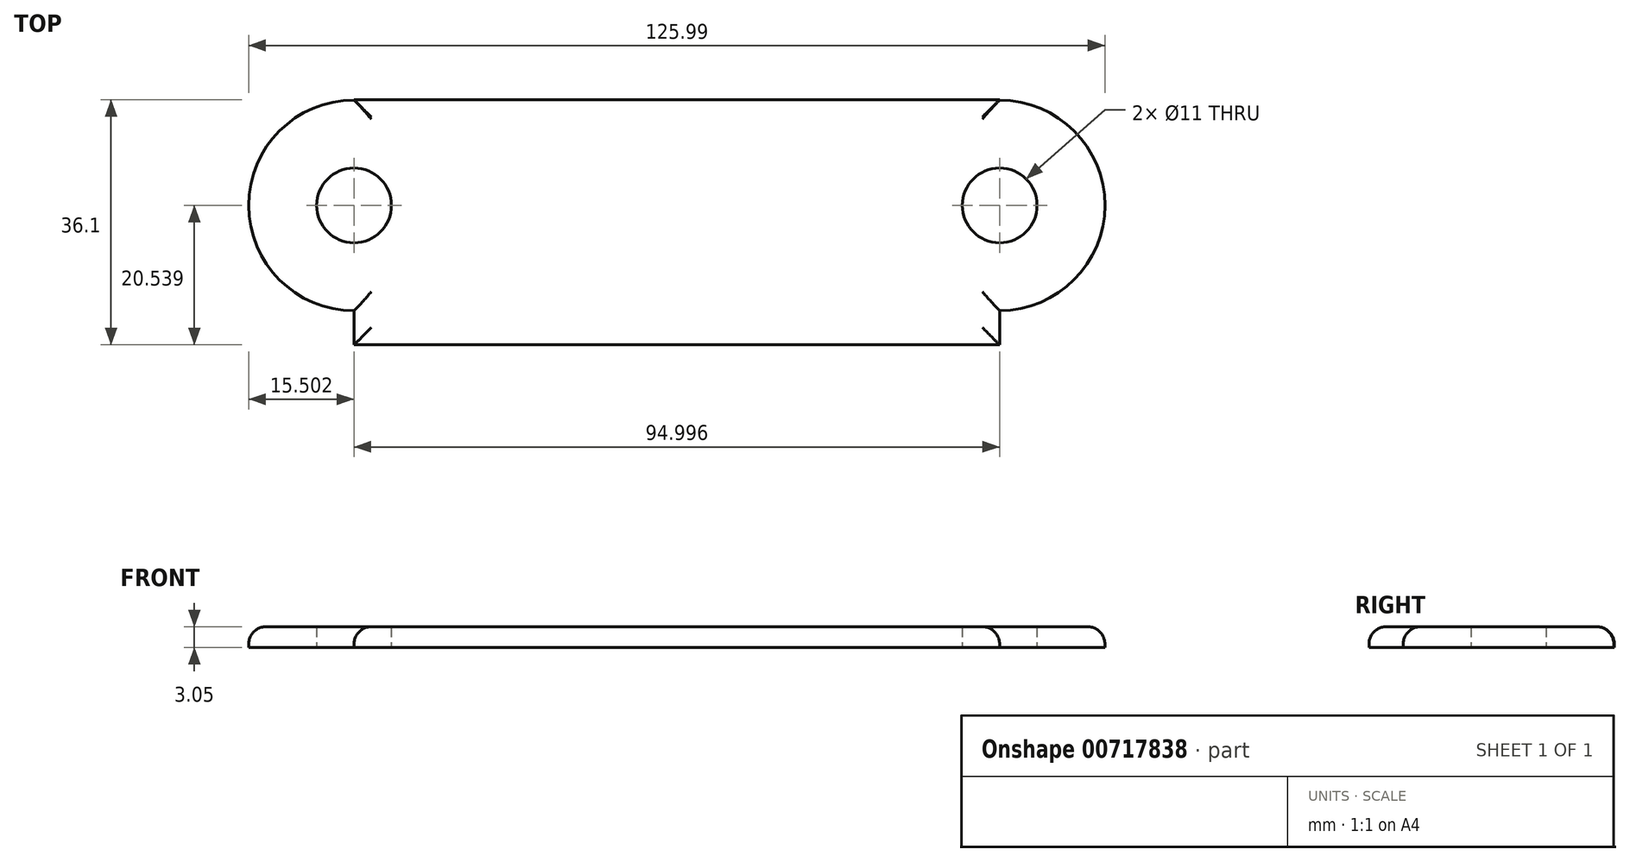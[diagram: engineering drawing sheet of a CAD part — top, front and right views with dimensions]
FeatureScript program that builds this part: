
annotation { "Feature Type Name" : "Feature", "Feature Type Description" : "" }
export const myFeature = defineFeature(function(context is Context, id is Id, definition is map)
    precondition{}
    {
        {
            var Q0;
            Q0=qCreatedBy(makeId("Top.planeOp"),FACE);
            var sketch = newSketch(context, id + "F0", { "sketchPlane" : qUnion([Q0])});
            skLineSegment(sketch, "E0.bottom", {"start": v(47.5, 18.05) * mm, "end": v(-47.5, 18.05) * mm});
            skLineSegment(sketch, "E0.top", {"start": v(47.5, -18.05) * mm, "end": v(-47.5, -18.05) * mm});
            skLineSegment(sketch, "E0.left", {"start": v(47.5, 18.05) * mm, "end": v(47.5, -18.05) * mm});
            skLineSegment(sketch, "E0.right", {"start": v(-47.5, 18.05) * mm, "end": v(-47.5, -18.05) * mm});
            skPoint(sketch, "E0.middle", {"position": v(0, 0) * mm});
            skCircle(sketch, "E1", {"center": v(-47.5, 2.49) * mm, "radius": 15.5 * mm});
            skCircle(sketch, "E2", {"center": v(47.5, 2.49) * mm, "radius": 15.5 * mm});
            skSolve(sketch);
        }
        {
            var Q0;
            Q0=qSketchRegion(id+"F0",true);
            extrude(context, id + "F1", {"entities" : qUnion([Q0]), "depth" : 3.05 * mm, "offsetDistance" : 25.4 * mm});
        }
        {
            var Q0;
            Q0=makeQuery(id+"F1.opExtrude","CAP_EDGE",EDGE,{"disambiguationData":[OSD([sQuery(id+"F0.wireOp",EDGE,"E1")])],"isStart":false});
            var Q1;
            Q1=makeQuery(id+"F1.opExtrude","CAP_EDGE",EDGE,{"disambiguationData":[OSD([sQuery(id+"F0.wireOp",EDGE,"E2")])],"isStart":false});
            var Q2;
            Q2=makeQuery(id+"F1.opExtrude","CAP_FACE",FACE,{"disambiguationData":[OSD([sQuery(id+"F0.wireOp",EDGE,"E0.bottom"),sQuery(id+"F0.wireOp",EDGE,"E0.top"),sQuery(id+"F0.wireOp",EDGE,"E0.left"),sQuery(id+"F0.wireOp",EDGE,"E0.right"),sQuery(id+"F0.wireOp",EDGE,"E1"),sQuery(id+"F0.wireOp",EDGE,"E2")])],"isStart":false});
            fillet(context, id + "F2", {"entities" : qUnion([Q0, Q1, Q2]), "radius" : 2.54 * mm, "tangentPropagation" : true, "allowEdgeOverflow" : false});
        }
        {
            var Q0;
            Q0=qCreatedBy(makeId("Top.planeOp"),FACE);
            var sketch = newSketch(context, id + "F3", { "sketchPlane" : qUnion([Q0])});
            skCircle(sketch, "E3", {"center": v(-47.5, 2.49) * mm, "radius": 5.5 * mm});
            skCircle(sketch, "E4", {"center": v(47.5, 2.49) * mm, "radius": 5.5 * mm});
            skSolve(sketch);
        }
        {
            var Q0;
            Q0=qSketchRegion(id+"F3",true);
            extrude(context, id + "F4", {"entities" : qUnion([Q0]), "operationType" : NewBodyOperationType.REMOVE, "depth" : 3.05 * mm, "offsetDistance" : 25.4 * mm});
        }
    });
